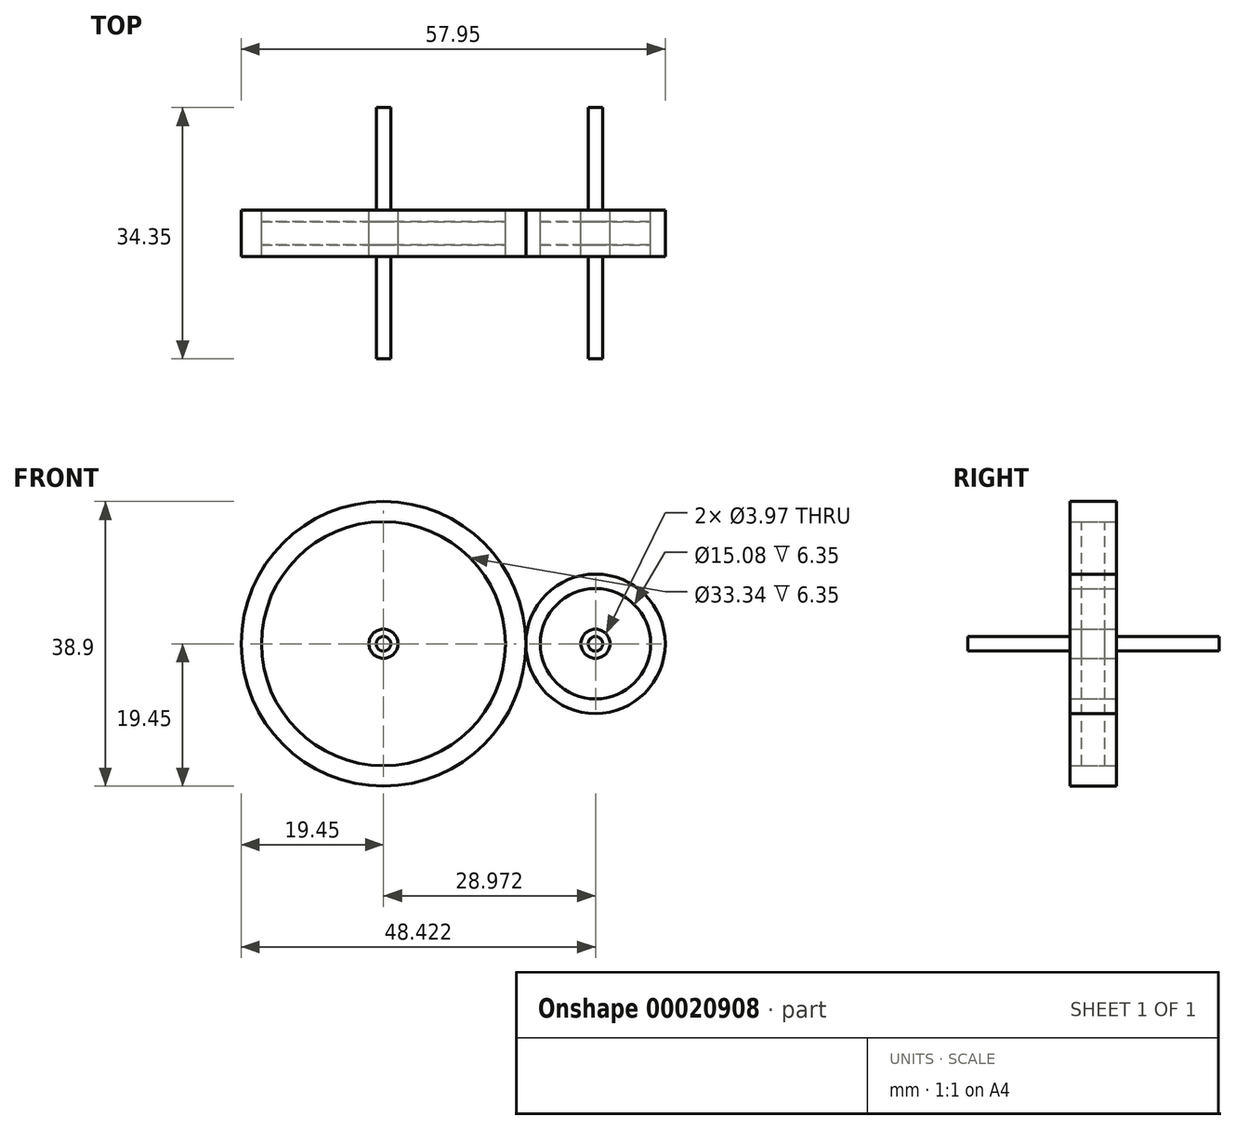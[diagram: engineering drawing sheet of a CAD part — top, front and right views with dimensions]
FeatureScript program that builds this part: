
annotation { "Feature Type Name" : "Feature", "Feature Type Description" : "" }
export const myFeature = defineFeature(function(context is Context, id is Id, definition is map)
    precondition{}
    {
        {
            var Q0;
            Q0=qCreatedBy(makeId("Front.planeOp"),FACE);
            var sketch = newSketch(context, id + "F0", { "sketchPlane" : qUnion([Q0])});
            skCircle(sketch, "E0", {"center": v(0, 0) * mm, "radius": 19.45 * mm});
            skCircle(sketch, "E1", {"center": v(0, 0) * mm, "radius": 1 * mm});
            skCircle(sketch, "E2", {"center": v(0, 0) * mm, "radius": 1.98 * mm});
            skCircle(sketch, "E3", {"center": v(0, 0) * mm, "radius": 16.67 * mm});
            skCircle(sketch, "E4", {"center": v(28.97, 0) * mm, "radius": 9.53 * mm});
            skCircle(sketch, "E5", {"center": v(28.97, 0) * mm, "radius": 1.98 * mm});
            skCircle(sketch, "E6", {"center": v(28.97, 0) * mm, "radius": 7.54 * mm});
            skCircle(sketch, "E7", {"center": v(28.97, 0) * mm, "radius": 1 * mm});
            skSolve(sketch);
        }
        {
            var Q0;
            Q0=makeQuery(id+"F0.imprint","IMPRINT",FACE,{"disambiguationData":[TD([[makeQuery(id+"F0.imprint","IMPRINT",EDGE,{"derivedFrom":sQuery(id+"F0.wireOp",EDGE,"E0")}),1.0]])]});
            var Q1;
            Q1=makeQuery(id+"F0.imprint","IMPRINT",FACE,{"disambiguationData":[TD([[makeQuery(id+"F0.imprint","IMPRINT",EDGE,{"derivedFrom":sQuery(id+"F0.wireOp",EDGE,"E4")}),1.0]])]});
            extrude(context, id + "F1", {"entities" : qUnion([Q0, Q1]), "depth" : 6.35 * mm});
        }
        {
            var Q0;
            Q0=makeQuery(id+"F0.imprint","IMPRINT",FACE,{"disambiguationData":[TD([[makeQuery(id+"F0.imprint","IMPRINT",EDGE,{"derivedFrom":sQuery(id+"F0.wireOp",EDGE,"E1")}),-1.0]])]});
            var Q1;
            Q1=makeQuery(id+"F0.imprint","IMPRINT",FACE,{"disambiguationData":[TD([[makeQuery(id+"F0.imprint","IMPRINT",EDGE,{"derivedFrom":sQuery(id+"F0.wireOp",EDGE,"E5")}),1.0]])]});
            extrude(context, id + "F2", {"entities" : qUnion([Q0, Q1]), "depth" : 6.35 * mm});
        }
        {
            var Q0;
            Q0=makeQuery(id+"F0.imprint","IMPRINT",FACE,{"disambiguationData":[TD([[makeQuery(id+"F0.imprint","IMPRINT",EDGE,{"derivedFrom":sQuery(id+"F0.wireOp",EDGE,"E2")}),-1.0]])]});
            var Q1;
            Q1=makeQuery(id+"F0.imprint","IMPRINT",FACE,{"disambiguationData":[TD([[makeQuery(id+"F0.imprint","IMPRINT",EDGE,{"derivedFrom":sQuery(id+"F0.wireOp",EDGE,"E5")}),-1.0]])]});
            extrude(context, id + "F3", {"entities" : qUnion([Q0, Q1]), "depth" : 4.76 * mm, "hasSecondDirection" : true, "secondDirectionOppositeDirection" : false, "secondDirectionDepth" : 1.59 * mm});
        }
        {
            var Q0;
            Q0=makeQuery(id+"F0.imprint","IMPRINT",FACE,{"disambiguationData":[TD([[makeQuery(id+"F0.imprint","IMPRINT",EDGE,{"derivedFrom":sQuery(id+"F0.wireOp",EDGE,"E1")}),1.0]])]});
            var Q1;
            Q1=makeQuery(id+"F0.imprint","IMPRINT",FACE,{"disambiguationData":[TD([[makeQuery(id+"F0.imprint","IMPRINT",EDGE,{"derivedFrom":sQuery(id+"F0.wireOp",EDGE,"E7")}),1.0]])]});
            extrude(context, id + "F4", {"entities" : qUnion([Q0, Q1]), "operationType" : NewBodyOperationType.ADD, "depth" : 14 * mm + 6.35 * mm, "hasSecondDirection" : true, "secondDirectionOppositeDirection" : true, "secondDirectionDepth" : 14 * mm});
        }
    });
